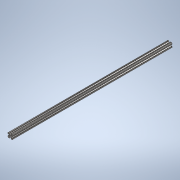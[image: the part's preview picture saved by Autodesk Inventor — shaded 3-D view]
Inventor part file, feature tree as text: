
AUTODESK INVENTOR PART (.ipt)
format: ipt  version: 2020 (Build 240168000, 168)  size: 246,272 bytes
history: native  units: in
note: dims shown in document units (in); Inventor stores cm internally (conversion verified against a paired STEP export)
features: extrude x1, sketch x1
ambient origin geometry x8: Origin, YZ Plane, XZ Plane, XY Plane, X Axis, Y Axis, Z Axis, Center Point
bodies: Solid1 (feature_tree)
feature tree (2):
  extrude  "Extrusion1"  [1 undecoded]
  sketch  "Sketch1"  dims[d0=35.0in d1=0.0in]
note: 1 required parameter value undecoded (feature->parameter linkage not recoverable at this tier; creation-order binding heuristic only, values carry confidence <= 0.55)
